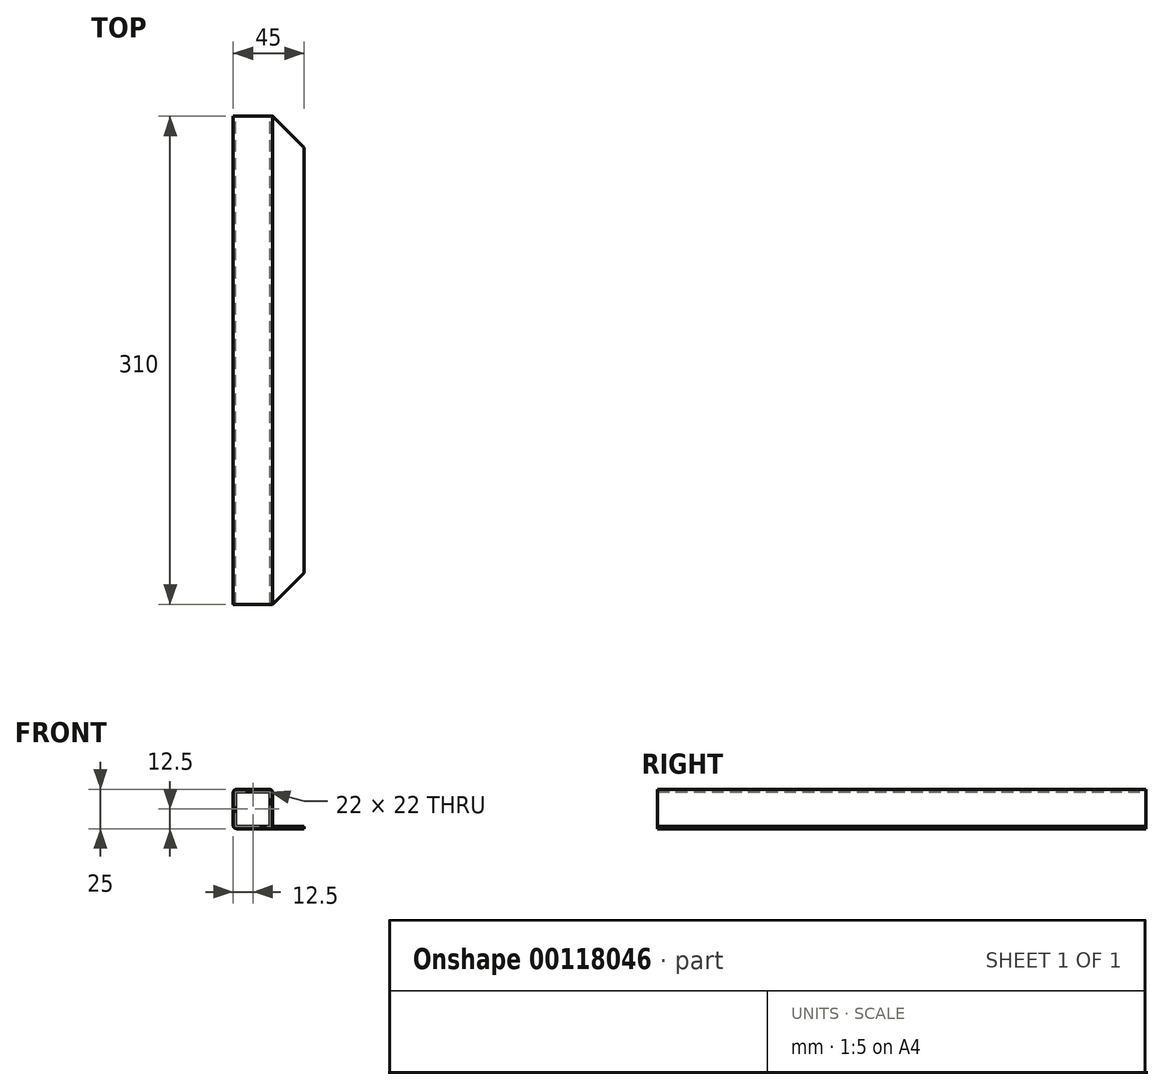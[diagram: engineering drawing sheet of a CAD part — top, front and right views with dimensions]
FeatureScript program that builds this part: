
annotation { "Feature Type Name" : "Feature", "Feature Type Description" : "" }
export const myFeature = defineFeature(function(context is Context, id is Id, definition is map)
    precondition{}
    {
        {
            var Q0;
            Q0=qCreatedBy(makeId("Front.planeOp"),FACE);
            var sketch = newSketch(context, id + "F0", { "sketchPlane" : qUnion([Q0])});
            skLineSegment(sketch, "E0.bottom", {"start": v(2, 0) * mm, "end": v(23, 0) * mm});
            skLineSegment(sketch, "E0.top", {"start": v(2, 25) * mm, "end": v(23, 25) * mm});
            skLineSegment(sketch, "E0.left", {"start": v(0, 2) * mm, "end": v(0, 23) * mm});
            skLineSegment(sketch, "E0.right", {"start": v(25, 2) * mm, "end": v(25, 23) * mm});
            skPoint(sketch, "E1.visualSharp", {"position": v(0, 25) * mm});
            skArc(sketch, "E1.filletArc", {"start": v(2, 25) * mm, "mid": v(0.59, 24.41) * mm, "end": v(0, 23) * mm});
            skPoint(sketch, "E2.visualSharp", {"position": v(25, 25) * mm});
            skArc(sketch, "E2.filletArc", {"start": v(25, 23) * mm, "mid": v(24.41, 24.41) * mm, "end": v(23, 25) * mm});
            skPoint(sketch, "E3.visualSharp", {"position": v(25, 0) * mm});
            skPoint(sketch, "E4.visualSharp", {"position": v(0, 0) * mm});
            skArc(sketch, "E4.filletArc", {"start": v(0, 2) * mm, "mid": v(0.59, 0.59) * mm, "end": v(2, 0) * mm});
            skLineSegment(sketch, "E5.0", {"start": v(1.5, 23.5) * mm, "end": v(23.5, 23.5) * mm});
            skLineSegment(sketch, "E5.1", {"start": v(1.5, 1.5) * mm, "end": v(1.5, 23.5) * mm});
            skLineSegment(sketch, "E5.2", {"start": v(1.5, 1.5) * mm, "end": v(23.5, 1.5) * mm});
            skLineSegment(sketch, "E5.3", {"start": v(23.5, 1.5) * mm, "end": v(23.5, 23.5) * mm});
            skLineSegment(sketch, "E6", {"start": v(25, 2) * mm, "end": v(25, 1.5) * mm});
            skLineSegment(sketch, "E7", {"start": v(25, 0) * mm, "end": v(23, 0) * mm});
            skLineSegment(sketch, "E8", {"start": v(25, 1.5) * mm, "end": v(45, 1.5) * mm});
            skLineSegment(sketch, "E9", {"start": v(45, 1.5) * mm, "end": v(45, 0) * mm});
            skLineSegment(sketch, "E10", {"start": v(45, 0) * mm, "end": v(25, 0) * mm});
            skSolve(sketch);
        }
        {
            var Q0;
            Q0=makeQuery(id+"F0.imprint","IMPRINT",FACE,{"disambiguationData":[TD([[makeQuery(id+"F0.imprint","IMPRINT",EDGE,{"derivedFrom":sQuery(id+"F0.wireOp",EDGE,"E0.bottom")}),1.0]])]});
            extrude(context, id + "F1", {"entities" : qUnion([Q0]), "depth" : 310 * mm});
        }
        {
            var Q0;
            Q0=makeQuery(id+"F1.opExtrude","SWEPT_FACE",FACE,{"disambiguationData":[OSD([sQuery(id+"F0.wireOp",EDGE,"E8")])]});
            var sketch = newSketch(context, id + "F2", { "sketchPlane" : qUnion([Q0])});
            skLineSegment(sketch, "E11", {"start": v(25, 0) * mm, "end": v(45, -20) * mm});
            skLineSegment(sketch, "E12", {"start": v(45, -20) * mm, "end": v(45, 0) * mm});
            skLineSegment(sketch, "E13", {"start": v(45, 0) * mm, "end": v(25, 0) * mm});
            skLineSegment(sketch, "E14", {"start": v(25, -310) * mm, "end": v(45, -290) * mm});
            skLineSegment(sketch, "E15", {"start": v(45, -290) * mm, "end": v(45, -310) * mm});
            skLineSegment(sketch, "E16", {"start": v(45, -310) * mm, "end": v(25, -310) * mm});
            skSolve(sketch);
        }
        {
            var Q0;
            Q0=makeQuery(id+"F2.imprint","IMPRINT",FACE,{"disambiguationData":[TD([[makeQuery(id+"F2.imprint","IMPRINT",EDGE,{"derivedFrom":sQuery(id+"F2.wireOp",EDGE,"E11")}),1.0]])]});
            var Q1;
            Q1 = qSketchRegion(id + "F2", true);
            extrude(context, id + "F3", {"entities" : qUnion([Q0, Q1]), "operationType" : NewBodyOperationType.REMOVE, "oppositeDirection" : true, "depth" : 25 * mm});
        }
    });
